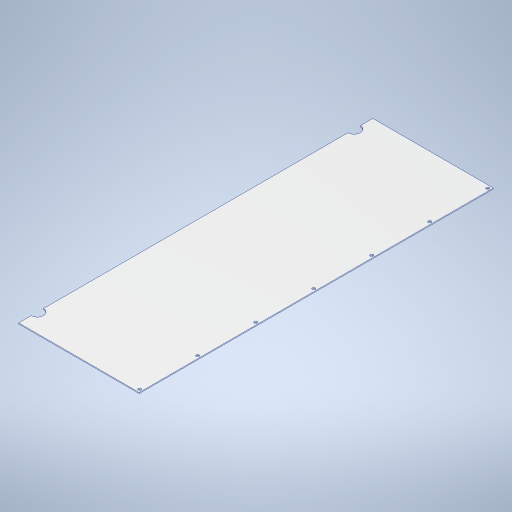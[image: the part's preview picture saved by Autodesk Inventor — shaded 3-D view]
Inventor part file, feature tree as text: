
AUTODESK INVENTOR PART (.ipt)
format: ipt  version: 2023 (Build 270158000, 158)  size: 262,144 bytes
history: native  units: in
note: dims shown in document units (in); Inventor stores cm internally (conversion verified against a paired STEP export)
features: sketch x3, hole x2, sheet_metal_op x1, pattern_linear x1, other x1
ambient origin geometry x8: Origin, YZ Plane, XZ Plane, XY Plane, X Axis, Y Axis, Z Axis, Center Point
bodies: Solid1 (feature_tree)
feature tree (8):
  sheet_metal_op  "Face1"
  hole  "Hole1"  [1 undecoded]
  pattern_linear  "Rectangular Pattern1"  Spacing1=0.0625in  [1 undecoded]
  hole  "Hole2"  [1 undecoded]
  sketch  "Sketch1"  dims[d0=7.6378in d1=22.4409in]
  other  "Plate1"
  sketch  "Sketch4"  dims[d2=3.8189in]
  sketch  "Sketch5"  dims[d3=11.2205in d4=0.0625in d15=0.194in d16=0.2953in d17=0.1476in d18=0.0984in d19=90.0deg d20=0.0625in d21=0.8108in d22=0.1939in d23=2.7559in d25=3.6755in d28=0.7874in d29=0.2953in d30=0.1476in d31=0.0984in d32=90.0deg d33=0.3937in d34=0.8108in d35=1.1811in d36=1.1811in d40=0.162in]
note: 3 required parameter values undecoded (feature->parameter linkage not recoverable at this tier; creation-order binding heuristic only, values carry confidence <= 0.55)
